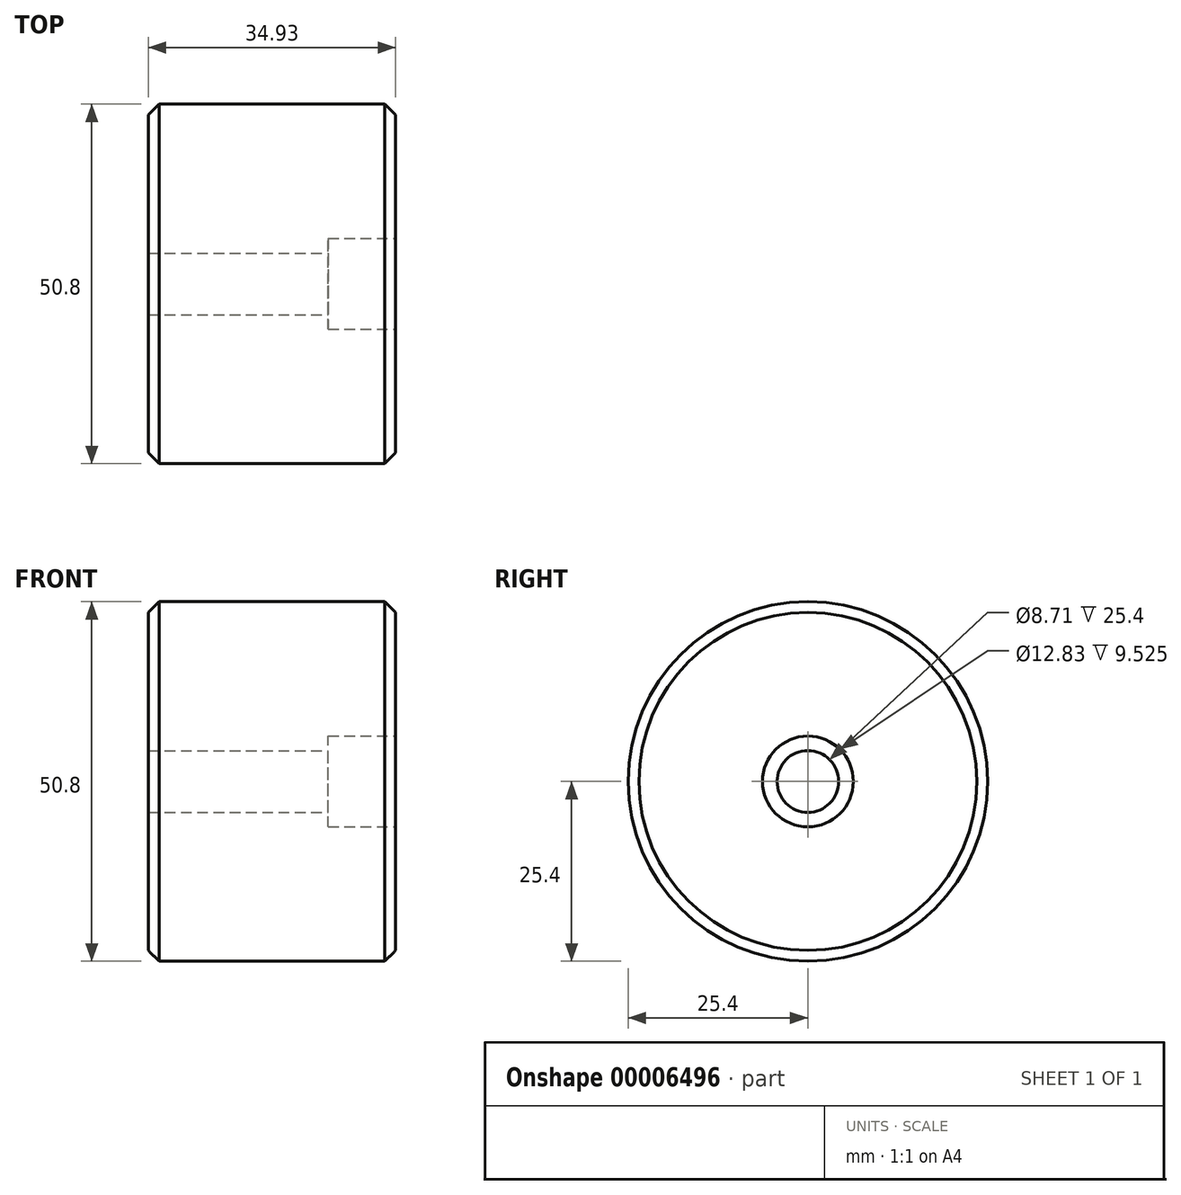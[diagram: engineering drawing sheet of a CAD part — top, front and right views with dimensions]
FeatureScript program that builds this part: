
annotation { "Feature Type Name" : "Feature", "Feature Type Description" : "" }
export const myFeature = defineFeature(function(context is Context, id is Id, definition is map)
    precondition{}
    {
        {
            var Q0;
            Q0=qCreatedBy(makeId("Right.planeOp"),FACE);
            var sketch = newSketch(context, id + "F0", { "sketchPlane" : qUnion([Q0])});
            skCircle(sketch, "E0", {"center": v(0, 0) * mm, "radius": 25.4 * mm});
            skSolve(sketch);
        }
        {
            var Q0;
            Q0 = qSketchRegion(id + "F0", true);
            extrude(context, id + "F1", {"entities" : qUnion([Q0]), "oppositeDirection" : true, "depth" : 34.92 * mm});
        }
        {
            var Q0;
            Q0=makeQuery(id+"F1.opExtrude","CAP_FACE",FACE,{"disambiguationData":[OSD([sQuery(id+"F0.wireOp",EDGE,"E0")])],"isStart":true});
            var sketch = newSketch(context, id + "F2", { "sketchPlane" : qUnion([Q0])});
            skCircle(sketch, "E1", {"center": v(0, 0) * mm, "radius": 4.36 * mm});
            skSolve(sketch);
        }
        {
            var Q0;
            Q0 = qSketchRegion(id + "F2", true);
            extrude(context, id + "F3", {"entities" : qUnion([Q0]), "operationType" : NewBodyOperationType.REMOVE, "endBound" : BoundingType.THROUGH_ALL, "oppositeDirection" : true, "depth" : 25.4 * mm});
        }
        {
            var Q0;
            Q0=makeQuery(id+"F1.opExtrude","CAP_EDGE",EDGE,{"disambiguationData":[OSD([sQuery(id+"F0.wireOp",EDGE,"E0")])],"isStart":true});
            var Q1;
            Q1=makeQuery(id+"F1.opExtrude","CAP_EDGE",EDGE,{"disambiguationData":[OSD([sQuery(id+"F0.wireOp",EDGE,"E0")])],"isStart":false});
            chamfer(context, id + "F4", {"entities" : qUnion([Q0, Q1]), "width" : 1.52 * mm, "tangentPropagation" : true});
        }
        {
            var Q0;
            Q0=makeQuery(id+"F1.opExtrude","CAP_FACE",FACE,{"disambiguationData":[OSD([sQuery(id+"F0.wireOp",EDGE,"E0")])],"isStart":true});
            var sketch = newSketch(context, id + "F5", { "sketchPlane" : qUnion([Q0])});
            skCircle(sketch, "E2", {"center": v(0, 0) * mm, "radius": 6.41 * mm});
            skSolve(sketch);
        }
        {
            var Q0;
            Q0 = qSketchRegion(id + "F5", true);
            extrude(context, id + "F6", {"entities" : qUnion([Q0]), "operationType" : NewBodyOperationType.REMOVE, "oppositeDirection" : true, "depth" : 9.52 * mm});
        }
    });
